# Revit family: QF_Summit_ACKDW721G_Kitchenette_with_Dishwasher_Refrigerator_Freezer
name_source: partatom
category: Specialty Equipment
units: mm (PartAtom-declared; Revit-internal decimal feet)

## family parameters
Always vertical = Yes
Cut with Voids When Loaded = No
Part Type = Normal
Room Calculation Point = No
Round Connector Dimension = Use Diameter
Shared = No
Work Plane-Based = No

## types (1)
- QF_Summit_ACKDW721G_Kitchenette_with_Dishwasher_Refrigerator_Freezer
    Apparent Power = 0 VA
    BTUH = 0.0 Btu/h
    Conn Conduit = Yes
    Cycle = 60 Hz
    Default Elevation = 0"
    Depth = 26"
    Description = Kichenette with Dishwasher & Refrigerator/Freezer
    Elec Conn Connection Height = 0"
    Elec Conn RI Height = 0"
    Electrical Remarks = 115 V cooktop
    FL Amps = 0 A
    Foodservice Equipment Identifier = Yes
    Height = 40"
    Identify Quantity as Lot = Yes
    Length = 71"
    Manufacturer = Summit
    Max Overcurrent Protection = 0 A
    Min Ckt Ampacity = 0 A
    Model = ACKDW721G
    Number of Poles = 1
    Phase = 1
    Refrigerant Type = R134a
    Refrigerant Volume = 0.00 kip
    Volts = 115 V
    Watts = 0 W
    Weight in Pounds = 300

## geometry (parser evidence)
native form markers: Sweep x11
no freeform markers — native parametric forms only
